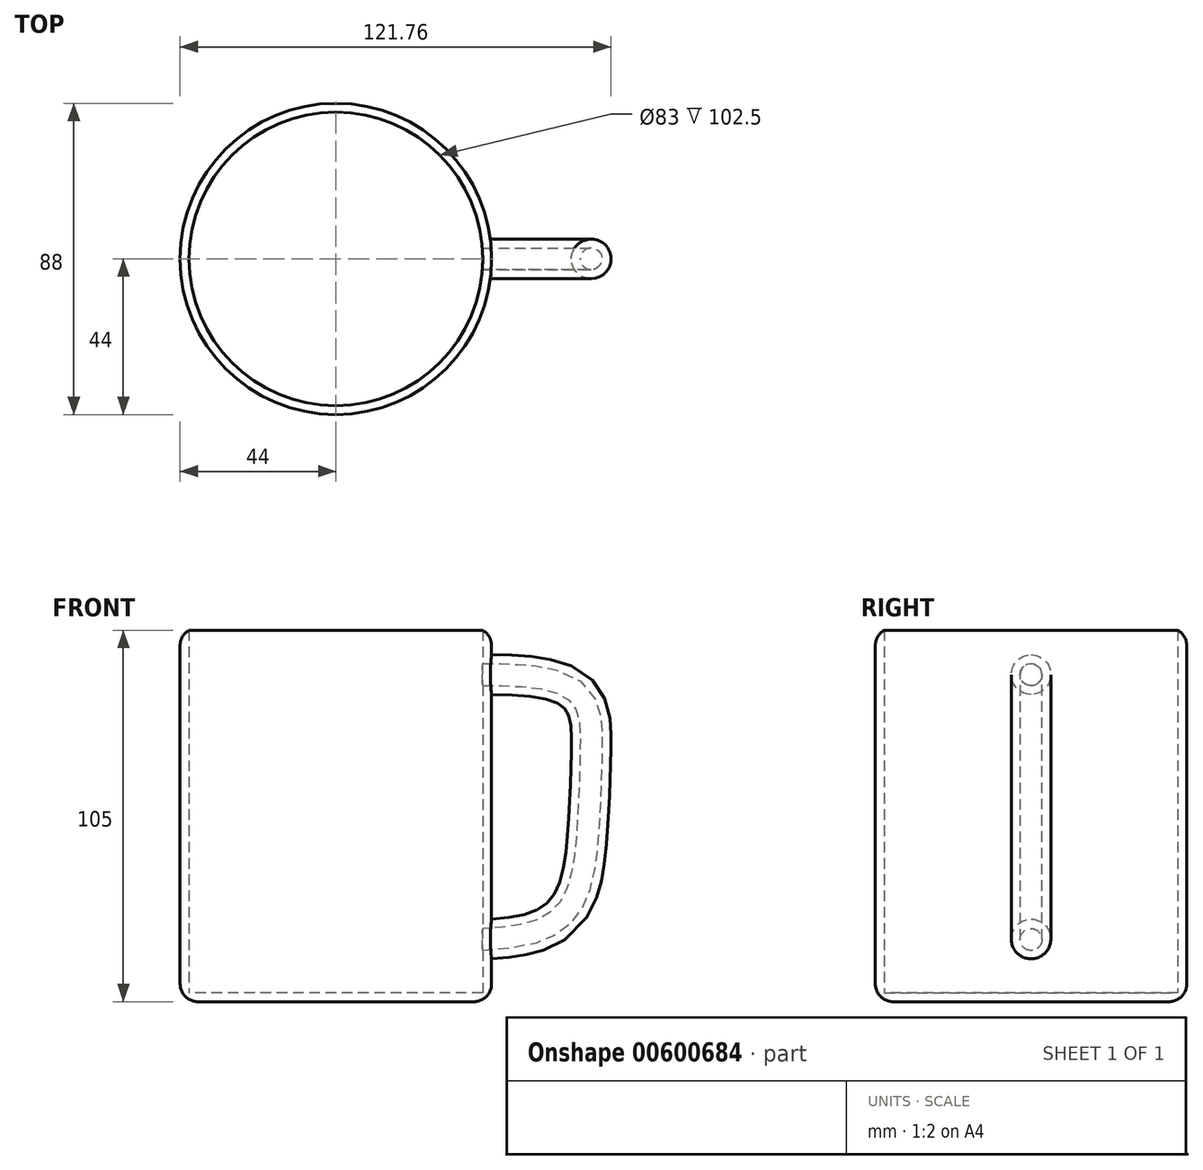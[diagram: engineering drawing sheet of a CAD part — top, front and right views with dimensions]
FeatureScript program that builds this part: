
annotation { "Feature Type Name" : "Feature", "Feature Type Description" : "" }
export const myFeature = defineFeature(function(context is Context, id is Id, definition is map)
    precondition{}
    {
        {
            var Q0;
            Q0=qCreatedBy(makeId("Top.planeOp"),FACE);
            var sketch = newSketch(context, id + "F0", { "sketchPlane" : qUnion([Q0])});
            skCircle(sketch, "E0", {"center": v(0, 0) * mm, "radius": 44 * mm});
            skSolve(sketch);
        }
        {
            var Q0;
            Q0 = qSketchRegion(id + "F0", true);
            extrude(context, id + "F1", {"entities" : qUnion([Q0]), "depth" : 105 * mm, "offsetDistance" : 25 * mm});
        }
        {
            var Q0;
            Q0=qCreatedBy(makeId("Front.planeOp"),FACE);
            var sketch = newSketch(context, id + "F2", { "sketchPlane" : qUnion([Q0])});
            skFitSpline(sketch, "E1", {"points": [v(36.99, 88.86) * mm, v(65.4, 85.03) * mm, v(68.56, 72.17) * mm, v(67.44, 46.46) * mm, v(60.9, 26.16) * mm, v(35.86, 20.98) * mm], "startDerivative": vector(157.2, 1.35) * mm, "endDerivative": vector(-138.97, -3.73) * mm});
            skSolve(sketch);
        }
        {
            var Q0;
            Q0=qCreatedBy(makeId("Right.planeOp"),FACE);
            cPlane(context, id + "F3", {"entities" : qUnion([Q0]), "cplaneType" : CPlaneType.OFFSET, "offset" : 44 * mm, "width" : 150 * mm, "height" : 150 * mm});
        }
        {
            var Q0;
            Q0=qCreatedBy(id+"F3.planeOp",FACE);
            var sketch = newSketch(context, id + "F4", { "sketchPlane" : qUnion([Q0])});
            skCircle(sketch, "E2", {"center": v(0, 92.47) * mm, "radius": 5.6 * mm});
            skSolve(sketch);
        }
        {
            var Q0;
            Q0 = qSketchRegion(id + "F4", true);
            var Q1;
            Q1=sQuery(id+"F2.wireOp",EDGE,"E1");
            sweep(context, id + "F5", {"operationType" : NewBodyOperationType.ADD, "profiles" : qUnion([Q0]), "path" : qUnion([Q1])});
        }
        {
            var Q0;
            Q0=makeQuery(id+"F1.opExtrude","CAP_FACE",FACE,{"disambiguationData":[OSD([sQuery(id+"F0.wireOp",EDGE,"E0")])],"isStart":false});
            shell(context, id + "F6", {"entities" : qUnion([Q0]), "thickness" : 2.5 * mm});
        }
        {
            var Q0;
            Q0=makeQuery(id+"F1.opExtrude","CAP_EDGE",EDGE,{"disambiguationData":[OSD([sQuery(id+"F0.wireOp",EDGE,"E0")])],"isStart":false});
            var Q1;
            Q1=makeQuery(id+"F1.opExtrude","CAP_EDGE",EDGE,{"disambiguationData":[OSD([sQuery(id+"F0.wireOp",EDGE,"E0")])],"isStart":true});
            fillet(context, id + "F7", {"entities" : qUnion([Q0, Q1]), "radius" : 5 * mm, "tangentPropagation" : true, "allowEdgeOverflow" : false});
        }
    });
